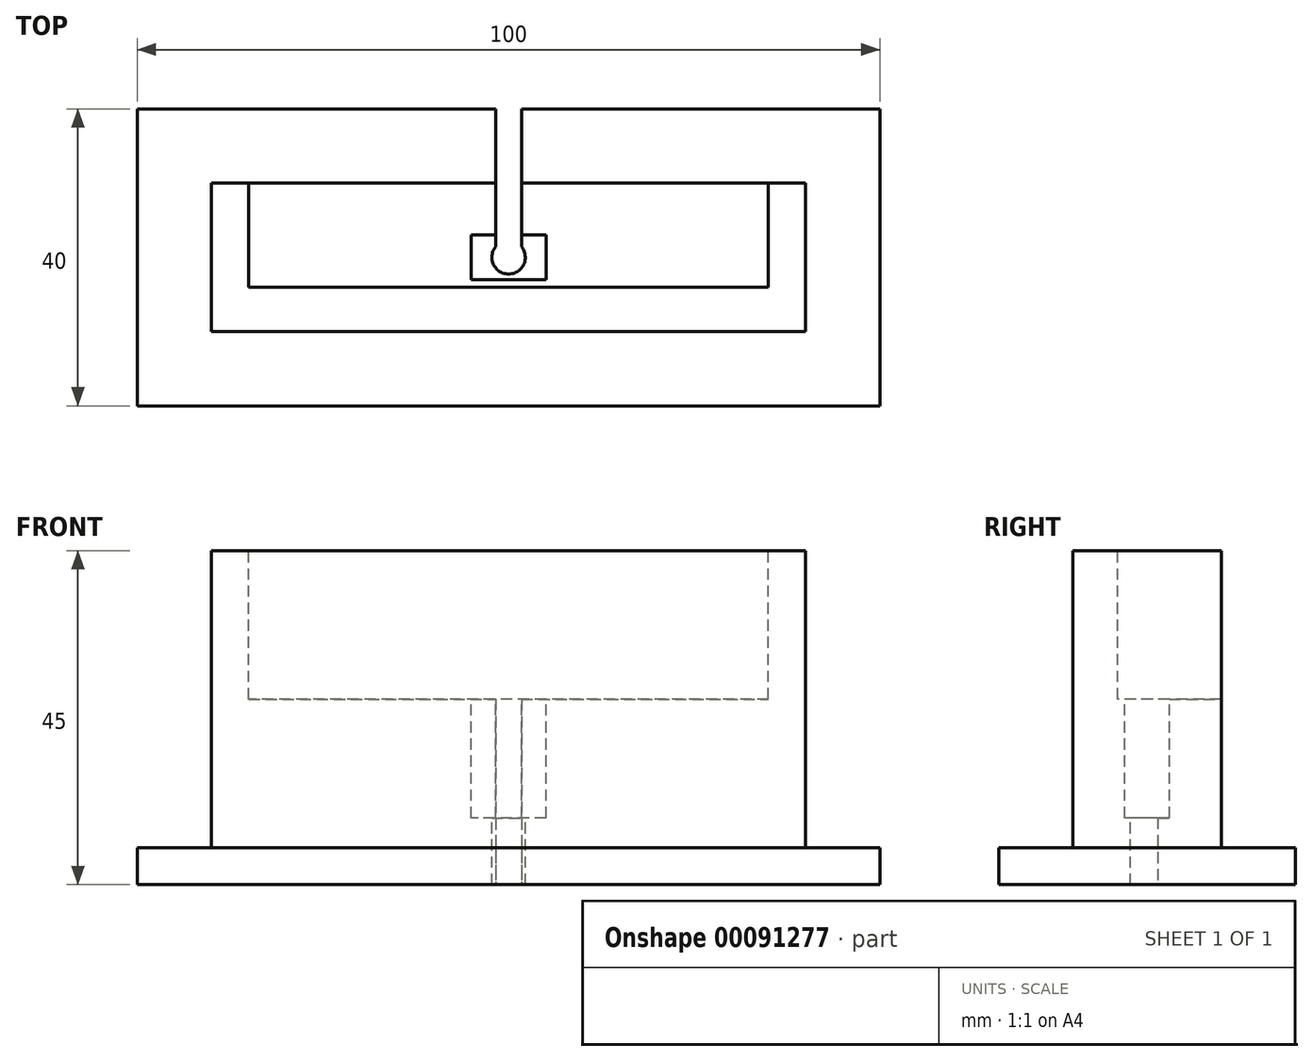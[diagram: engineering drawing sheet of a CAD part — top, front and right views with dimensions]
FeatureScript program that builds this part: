
annotation { "Feature Type Name" : "Feature", "Feature Type Description" : "" }
export const myFeature = defineFeature(function(context is Context, id is Id, definition is map)
    precondition{}
    {
        {
            var Q0;
            Q0=qCreatedBy(makeId("Top.planeOp"),FACE);
            var sketch = newSketch(context, id + "F0", { "sketchPlane" : qUnion([Q0])});
            skLineSegment(sketch, "E0.bottom", {"start": v(5.05, 3) * mm, "end": v(-5.05, 3) * mm});
            skLineSegment(sketch, "E0.top", {"start": v(5.05, -3) * mm, "end": v(-5.05, -3) * mm});
            skLineSegment(sketch, "E0.left", {"start": v(5.05, 3) * mm, "end": v(5.05, -3) * mm});
            skLineSegment(sketch, "E0.right", {"start": v(-5.05, 3) * mm, "end": v(-5.05, -3) * mm});
            skPoint(sketch, "E0.middle", {"position": v(0, 0) * mm});
            skCircle(sketch, "E1", {"center": v(0, 0) * mm, "radius": 2.25 * mm});
            skLineSegment(sketch, "E2.bottom", {"start": v(35, 4) * mm, "end": v(-35, 4) * mm});
            skLineSegment(sketch, "E2.top", {"start": v(35, -4) * mm, "end": v(-35, -4) * mm});
            skLineSegment(sketch, "E2.left", {"start": v(35, 4) * mm, "end": v(35, -4) * mm});
            skLineSegment(sketch, "E2.right", {"start": v(-35, 4) * mm, "end": v(-35, -4) * mm});
            skLineSegment(sketch, "E3.bottom", {"start": v(-40, -10) * mm, "end": v(40, -10) * mm});
            skLineSegment(sketch, "E3.top", {"start": v(-40, 10) * mm, "end": v(40, 10) * mm});
            skLineSegment(sketch, "E3.left", {"start": v(-40, -10) * mm, "end": v(-40, 10) * mm});
            skLineSegment(sketch, "E3.right", {"start": v(40, -10) * mm, "end": v(40, 10) * mm});
            skLineSegment(sketch, "E4.bottom", {"start": v(-50, 20) * mm, "end": v(50, 20) * mm});
            skLineSegment(sketch, "E4.top", {"start": v(-50, -20) * mm, "end": v(50, -20) * mm});
            skLineSegment(sketch, "E4.left", {"start": v(-50, 20) * mm, "end": v(-50, -20) * mm});
            skLineSegment(sketch, "E4.right", {"start": v(50, 20) * mm, "end": v(50, -20) * mm});
            skLineSegment(sketch, "E5", {"start": v(-1.75, 0) * mm, "end": v(-1.75, 20) * mm});
            skLineSegment(sketch, "E6", {"start": v(1.75, 0) * mm, "end": v(1.75, 20) * mm});
            skPoint(sketch, "E6.startSnap0", {"position": v(5.05, 0) * mm});
            skSolve(sketch);
        }
        {
            var Q0;
            Q0=makeQuery(id+"F0.imprint","IMPRINT",FACE,{"disambiguationData":[TD([[makeQuery(id+"F0.imprint","IMPRINT",EDGE,{"derivedFrom":sQuery(id+"F0.wireOp",EDGE,"E3.bottom")}),-1.0]])]});
            var Q1;
            Q1=makeQuery(id+"F0.imprint","IMPRINT",FACE,{"disambiguationData":[TD([[makeQuery(id+"F0.imprint","IMPRINT",EDGE,{"derivedFrom":sQuery(id+"F0.wireOp",EDGE,"E2.bottom")}),-1.0]])]});
            var Q2;
            Q2=makeQuery(id+"F0.imprint","IMPRINT",FACE,{"disambiguationData":[TD([[makeQuery(id+"F0.imprint","IMPRINT",EDGE,{"derivedFrom":sQuery(id+"F0.wireOp",EDGE,"E0.bottom")}),-1.0]])]});
            var Q3;
            Q3=makeQuery(id+"F0.imprint","IMPRINT",FACE,{"disambiguationData":[TD([[makeQuery(id+"F0.imprint","IMPRINT",EDGE,{"derivedFrom":sQuery(id+"F0.wireOp",EDGE,"E0.bottom")}),1.0]])]});
            var Q4;
            Q4=makeQuery(id+"F0.imprint","IMPRINT",FACE,{"disambiguationData":[TD([[makeQuery(id+"F0.imprint","IMPRINT",EDGE,{"derivedFrom":sQuery(id+"F0.wireOp",EDGE,"E1")}),1.0]])]});
            extrude(context, id + "F1", {"entities" : qUnion([Q0, Q1, Q2, Q3, Q4]), "depth" : 5 * mm});
        }
        {
            var Q0;
            Q0=makeQuery(id+"F1.opExtrude","CAP_FACE",FACE,{"disambiguationData":[OSD([sQuery(id+"F0.wireOp",EDGE,"E4.bottom"),sQuery(id+"F0.wireOp",EDGE,"E4.top"),sQuery(id+"F0.wireOp",EDGE,"E4.left"),sQuery(id+"F0.wireOp",EDGE,"E4.right")])],"isStart":false});
            var sketch = newSketch(context, id + "F2", { "sketchPlane" : qUnion([Q0])});
            skLineSegment(sketch, "E7.0", {"start": v(-40, -10) * mm, "end": v(40, -10) * mm});
            skLineSegment(sketch, "E7.1", {"start": v(-40, -10) * mm, "end": v(-40, 10) * mm});
            skLineSegment(sketch, "E7.2", {"start": v(-40, 10) * mm, "end": v(40, 10) * mm});
            skLineSegment(sketch, "E7.3", {"start": v(40, -10) * mm, "end": v(40, 10) * mm});
            skSolve(sketch);
        }
        {
            var Q0;
            Q0=makeQuery(id+"F2.imprint","IMPRINT",FACE,{"disambiguationData":[TD([[makeQuery(id+"F2.imprint","IMPRINT",EDGE,{"derivedFrom":sQuery(id+"F2.wireOp",EDGE,"E7.0")}),1.0]])]});
            extrude(context, id + "F3", {"entities" : qUnion([Q0]), "operationType" : NewBodyOperationType.ADD, "depth" : 40 * mm});
        }
        {
            var Q0;
            Q0=makeQuery(id+"F3.opExtrude","CAP_FACE",FACE,{"disambiguationData":[OSD([sQuery(id+"F2.wireOp",EDGE,"E7.0"),sQuery(id+"F2.wireOp",EDGE,"E7.1"),sQuery(id+"F2.wireOp",EDGE,"E7.2"),sQuery(id+"F2.wireOp",EDGE,"E7.3")])],"isStart":false});
            var sketch = newSketch(context, id + "F4", { "sketchPlane" : qUnion([Q0])});
            skLineSegment(sketch, "E8.0", {"start": v(35, -4) * mm, "end": v(-35, -4) * mm});
            skLineSegment(sketch, "E8.1", {"start": v(-35, 4) * mm, "end": v(-35, -4) * mm});
            skLineSegment(sketch, "E8.2", {"start": v(35, 4) * mm, "end": v(-35, 4) * mm});
            skLineSegment(sketch, "E8.3", {"start": v(35, 4) * mm, "end": v(35, -4) * mm});
            skSolve(sketch);
        }
        {
            var Q0;
            Q0=makeQuery(id+"F4.imprint","IMPRINT",FACE,{"disambiguationData":[TD([[makeQuery(id+"F4.imprint","IMPRINT",EDGE,{"derivedFrom":sQuery(id+"F4.wireOp",EDGE,"E8.0")}),-1.0]])]});
            extrude(context, id + "F5", {"entities" : qUnion([Q0]), "operationType" : NewBodyOperationType.REMOVE, "oppositeDirection" : true, "depth" : 20 * mm});
        }
        {
            var Q0;
            Q0=makeQuery(id+"F5.boolean.opBoolean","COPY",FACE,{"derivedFrom":makeQuery(id+"F5.opExtrude","CAP_FACE",FACE,{"disambiguationData":[OSD([sQuery(id+"F4.wireOp",EDGE,"E8.0"),sQuery(id+"F4.wireOp",EDGE,"E8.1"),sQuery(id+"F4.wireOp",EDGE,"E8.2"),sQuery(id+"F4.wireOp",EDGE,"E8.3")])],"isStart":false})});
            var sketch = newSketch(context, id + "F6", { "sketchPlane" : qUnion([Q0])});
            skLineSegment(sketch, "E9.0", {"start": v(5.05, 3) * mm, "end": v(5.05, -3) * mm});
            skLineSegment(sketch, "E9.1", {"start": v(5.05, 3) * mm, "end": v(-5.05, 3) * mm});
            skLineSegment(sketch, "E9.2", {"start": v(-5.05, 3) * mm, "end": v(-5.05, -3) * mm});
            skLineSegment(sketch, "E9.3", {"start": v(5.05, -3) * mm, "end": v(-5.05, -3) * mm});
            skCircle(sketch, "E9.4", {"center": v(0, 0) * mm, "radius": 2.25 * mm});
            skSolve(sketch);
        }
        {
            var Q0;
            Q0=makeQuery(id+"F6.imprint","IMPRINT",FACE,{"disambiguationData":[TD([[makeQuery(id+"F6.imprint","IMPRINT",EDGE,{"derivedFrom":sQuery(id+"F6.wireOp",EDGE,"E9.0")}),-1.0]])]});
            extrude(context, id + "F7", {"entities" : qUnion([Q0]), "operationType" : NewBodyOperationType.REMOVE, "oppositeDirection" : true, "depth" : 16 * mm});
        }
        {
            var Q0;
            Q0=makeQuery(id+"F7.boolean.opBoolean","SPLIT",FACE,{"disambiguationData":[TD([makeQuery(id+"F7.opExtrude","SWEPT_FACE",FACE,{"disambiguationData":[OSD([sQuery(id+"F6.wireOp",EDGE,"E9.4")])]})])],"derivedFrom":makeQuery(id+"F5.boolean.opBoolean","COPY",FACE,{"derivedFrom":makeQuery(id+"F5.opExtrude","CAP_FACE",FACE,{"disambiguationData":[OSD([sQuery(id+"F4.wireOp",EDGE,"E8.0"),sQuery(id+"F4.wireOp",EDGE,"E8.1"),sQuery(id+"F4.wireOp",EDGE,"E8.2"),sQuery(id+"F4.wireOp",EDGE,"E8.3")])],"isStart":false})})});
            extrude(context, id + "F8", {"entities" : qUnion([Q0]), "operationType" : NewBodyOperationType.REMOVE, "oppositeDirection" : true, "depth" : 25 * mm});
        }
        {
            var Q0;
            {var subQ5=sQuery(id+"F6.wireOp",EDGE,"E9.0");Q0=makeQuery(id+"F6.imprint","IMPRINT",FACE,{"disambiguationData":[TD([[makeQuery(id+"F6.imprint","IMPRINT",EDGE,{"derivedFrom":subQ5}),1.0]])]});}
            var sketch = newSketch(context, id + "F9", { "sketchPlane" : qUnion([Q0])});
            skLineSegment(sketch, "E10.0", {"start": v(-35, 4) * mm, "end": v(-35, -4) * mm});
            skLineSegment(sketch, "E10.1", {"start": v(35, 4) * mm, "end": v(35, -4) * mm});
            skLineSegment(sketch, "E11.0", {"start": v(-50, 20) * mm, "end": v(50, 20) * mm});
            skLineSegment(sketch, "E12", {"start": v(-35, 4) * mm, "end": v(-35, 20) * mm});
            skLineSegment(sketch, "E13", {"start": v(35, 4) * mm, "end": v(35, 20) * mm});
            skLineSegment(sketch, "E14.0", {"start": v(35, 4) * mm, "end": v(-35, 4) * mm});
            skLineSegment(sketch, "E15.0", {"start": v(1.75, 20) * mm, "end": v(50, 20) * mm});
            skLineSegment(sketch, "E15.1", {"start": v(-50, 20) * mm, "end": v(-1.75, 20) * mm});
            skSolve(sketch);
        }
        {
            var Q0;
            {var subQ9=sQuery(id+"F9.wireOp",EDGE,"E11.0");Q0=makeQuery(id+"F9.imprint","IMPRINT",FACE,{"disambiguationData":[TD([[makeQuery(id+"F9.imprint","IMPRINT",EDGE,{"derivedFrom":subQ9}),-1.0]])]});}
            extrude(context, id + "F10", {"entities" : qUnion([Q0]), "operationType" : NewBodyOperationType.REMOVE, "depth" : 25 * mm});
        }
    });
